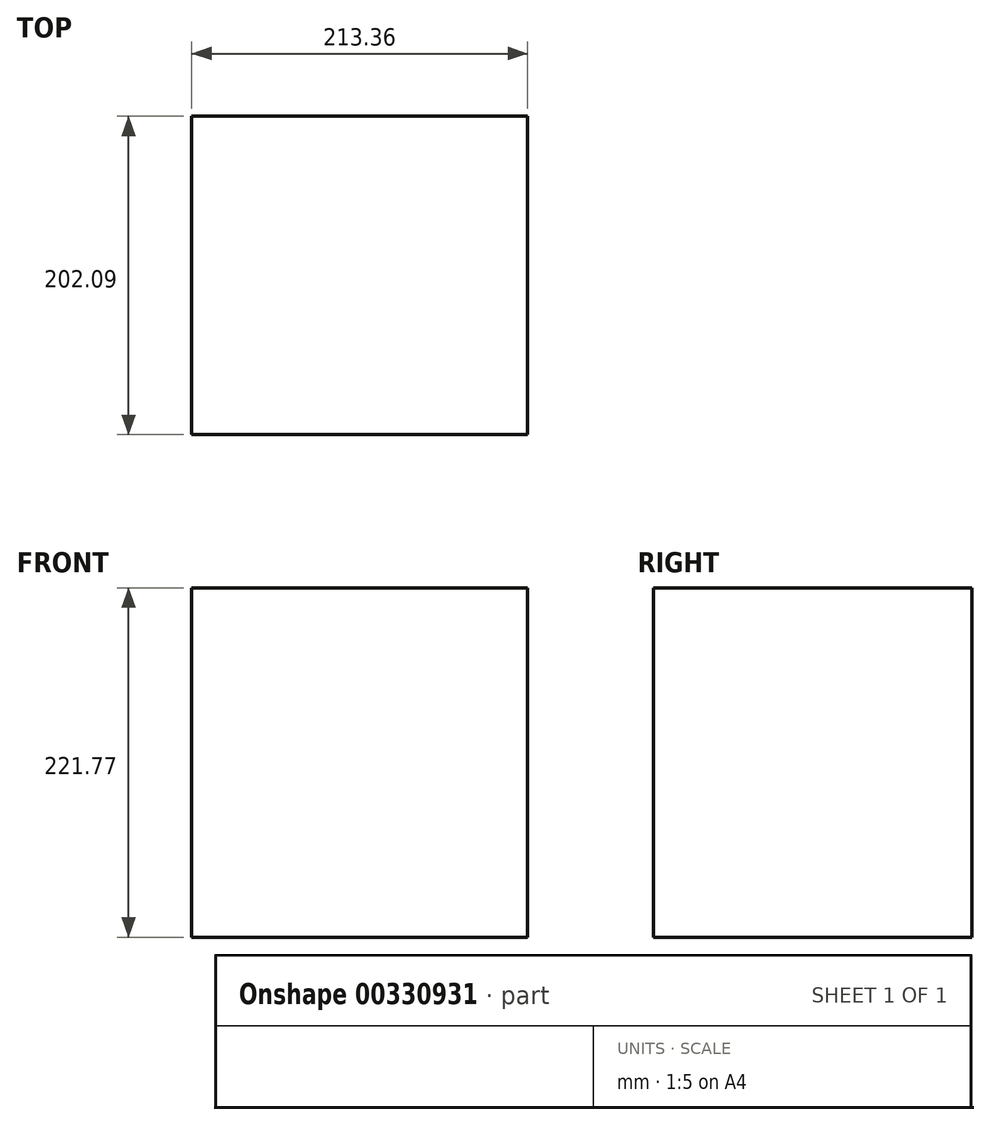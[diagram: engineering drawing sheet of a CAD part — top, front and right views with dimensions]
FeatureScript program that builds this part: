
annotation { "Feature Type Name" : "Feature", "Feature Type Description" : "" }
export const myFeature = defineFeature(function(context is Context, id is Id, definition is map)
    precondition{}
    {
        {
            var Q0;
            Q0=qCreatedBy(makeId("Top.planeOp"),FACE);
            var sketch = newSketch(context, id + "F0", { "sketchPlane" : qUnion([Q0])});
            skLineSegment(sketch, "E0.bottom", {"start": v(-95.51, -95.56) * mm, "end": v(117.85, -95.56) * mm});
            skLineSegment(sketch, "E0.top", {"start": v(-95.51, 106.53) * mm, "end": v(117.85, 106.53) * mm});
            skLineSegment(sketch, "E0.left", {"start": v(-95.51, -95.56) * mm, "end": v(-95.51, 106.53) * mm});
            skLineSegment(sketch, "E0.right", {"start": v(117.85, -95.56) * mm, "end": v(117.85, 106.53) * mm});
            skSolve(sketch);
        }
        {
            var Q0;
            Q0 = qSketchRegion(id + "F0", true);
            extrude(context, id + "F1", {"entities" : qUnion([Q0]), "depth" : 221.77 * mm});
        }
    });
